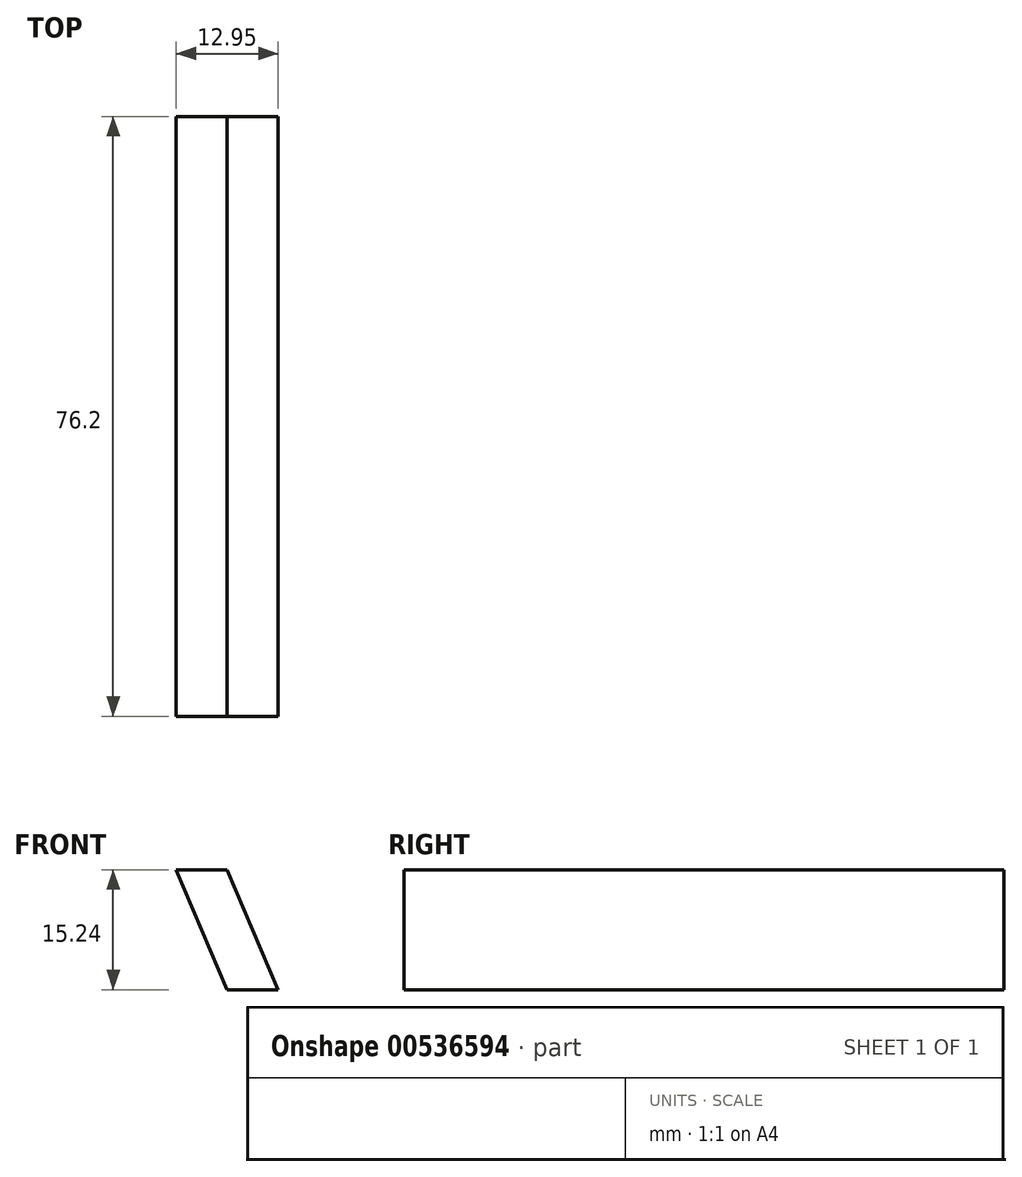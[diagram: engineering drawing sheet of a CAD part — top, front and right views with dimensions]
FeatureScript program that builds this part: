
annotation { "Feature Type Name" : "Feature", "Feature Type Description" : "" }
export const myFeature = defineFeature(function(context is Context, id is Id, definition is map)
    precondition{}
    {
        {
            var Q0;
            Q0=qCreatedBy(makeId("Front.planeOp"),FACE);
            var sketch = newSketch(context, id + "F0", { "sketchPlane" : qUnion([Q0])});
            skLineSegment(sketch, "E0.bottom", {"start": v(-15.3, -10.66) * mm, "end": v(-15.3, -10.66) * mm});
            skLineSegment(sketch, "E0.top", {"start": v(-15.3, -25.9) * mm, "end": v(-15.3, -25.9) * mm});
            skLineSegment(sketch, "E0.left", {"start": v(-15.3, -10.66) * mm, "end": v(-15.3, -25.9) * mm});
            skLineSegment(sketch, "E0.right", {"start": v(-15.3, -10.66) * mm, "end": v(-15.3, -25.9) * mm});
            skLineSegment(sketch, "E1", {"start": v(-15.3, -10.66) * mm, "end": v(-8.83, -25.9) * mm});
            skLineSegment(sketch, "E2", {"start": v(-8.83, -25.9) * mm, "end": v(-15.3, -25.9) * mm});
            skLineSegment(sketch, "E3", {"start": v(-15.3, -25.9) * mm, "end": v(-21.78, -10.66) * mm});
            skLineSegment(sketch, "E4", {"start": v(-15.3, -10.66) * mm, "end": v(-21.78, -10.66) * mm});
            skSolve(sketch);
        }
        {
            var Q0;
            Q0 = qSketchRegion(id + "F0", true);
            extrude(context, id + "F1", {"entities" : qUnion([Q0]), "depth" : 76.2 * mm, "offsetDistance" : 25.4 * mm});
        }
    });
